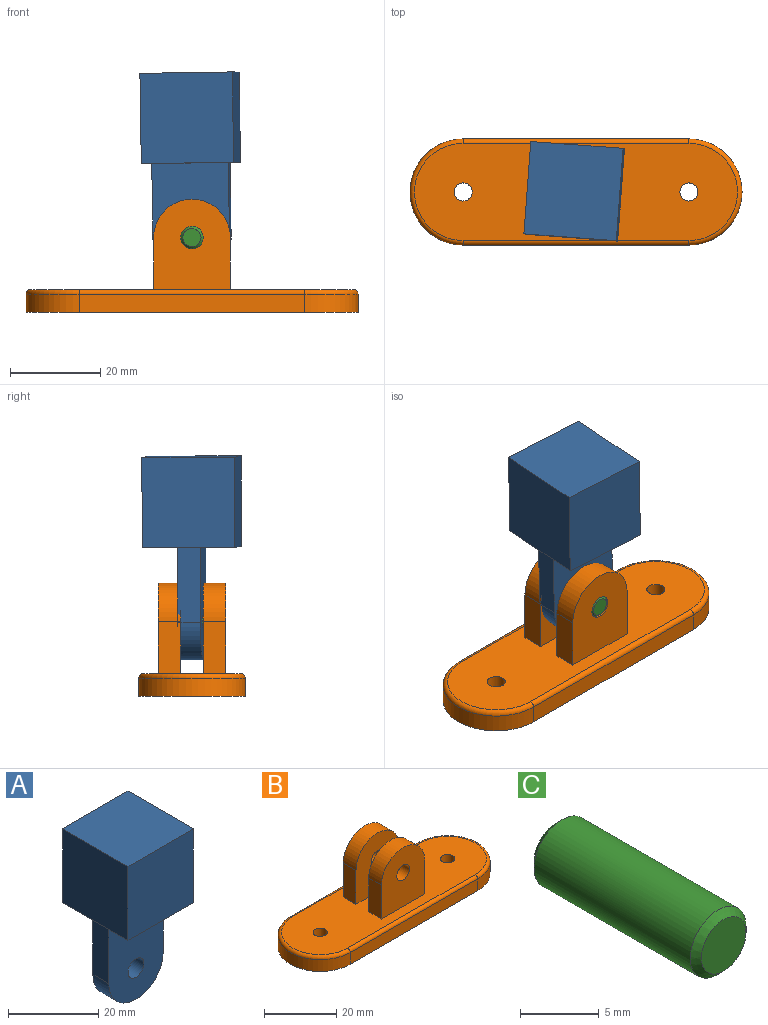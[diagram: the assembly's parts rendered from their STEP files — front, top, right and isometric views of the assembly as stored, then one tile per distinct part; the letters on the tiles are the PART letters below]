
ASSEMBLY  parts=3 mates=2
PART A: 12 faces, bbox 20.5x20.5x45 mm
  f0: plane 25x17mm, normal (0,-1,0), area 374.4mm2, adj f2,f3,f4,f10,f11
  f1: plane 25x17mm, normal (0,1,0), area 374.4mm2, adj f2,f3,f4,f10,f11
  f2: plane 16.5x5mm, normal (-1,0,0), area 82.5mm2, adj f0,f1,f4,f10
  f3: plane 16.5x5mm, normal (1,0,0), area 82.5mm2, adj f0,f1,f4,f10
  f4: plane 20.5x20.5mm, normal (0,0,-1), area 335.3mm2, adj f0,f1,f2,f3,f5,f6,f7,f8
  f5: plane 20.5x20mm, normal (0,-1,0), area 410mm2, adj f4,f6,f8,f9
  f6: plane 20.5x20mm, normal (1,0,0), area 410mm2, adj f4,f5,f7,f9
  f7: plane 20.5x20mm, normal (0,1,0), area 410mm2, adj f4,f6,f8,f9
  f8: plane 20.5x20mm, normal (-1,0,0), area 410mm2, adj f4,f5,f7,f9
  f9: plane 20.5x20.5mm, normal (0,0,1), area 420.3mm2, adj f5,f6,f7,f8
  f10: cylinder r=8.5mm len=17mm, axis (0,1,0), area 133.5mm2, adj f0,f1,f2,f3
  f11: cylinder r=2.5mm len=5mm, axis (0,1,0), area 78.5mm2, adj f0,f1
PART B: 24 faces, bbox 75.4x25.4x25 mm
  f0: plane 20x17mm, normal (0,-1,0), area 289.4mm2, adj f2,f3,f10,f21,f23
  f1: plane 20x17mm, normal (0,1,0), area 289.4mm2, adj f10,f17,f19,f20,f22
  f2: plane 11.5x5mm, normal (-1,0,0), area 57.5mm2, adj f0,f10,f16,f21
  f3: plane 11.5x5mm, normal (1,0,0), area 57.5mm2, adj f0,f10,f16,f21
  f4: plane 50x4mm, normal (0,1,0), area 200mm2, adj f5,f8,f11,f12
  f5: cylinder r=11.75mm len=23.5mm, axis (0,0,-1), area 147.7mm2, adj f4,f6,f11,f14
  f6: plane 50x4mm, normal (0,-1,0), area 200mm2, adj f5,f8,f11,f15
  f7: cylinder r=2mm len=5mm, axis (0,0,-1), area 62.8mm2, adj f10,f11
  f8: cylinder r=11.75mm len=23.5mm, axis (0,0,-1), area 147.7mm2, adj f4,f6,f11,f13
  f9: cylinder r=2mm len=5mm, axis (0,0,-1), area 62.8mm2, adj f10,f11
  f10: plane 71.5x21.5mm, normal (0,0,1), area 1242.9mm2, adj f0,f1,f2,f3,f7,f9,f12,f13
  f11: plane 73.5x23.5mm, normal (0,0,-1), area 1583.6mm2, adj f4,f5,f6,f7,f8,f9
  f12: cylinder r=1mm len=50mm, axis (1,0,0), area 78.5mm2, adj f4,f10,f13,f14
  f13: torus R=10.75mm, axis (0,0,1), area 56.2mm2, adj f8,f10,f12,f15
  f14: torus R=10.75mm, axis (0,0,1), area 56.2mm2, adj f5,f10,f12,f15
  f15: cylinder r=1mm len=50mm, axis (-1,0,0), area 78.5mm2, adj f6,f10,f13,f14
  f16: plane 20x17mm, normal (0,1,0), area 289.4mm2, adj f2,f3,f10,f21,f23
  f17: plane 11.5x5mm, normal (1,0,0), area 57.5mm2, adj f1,f10,f18,f20
  f18: plane 20x17mm, normal (0,-1,0), area 289.4mm2, adj f10,f17,f19,f20,f22
  f19: plane 11.5x5mm, normal (-1,0,0), area 57.5mm2, adj f1,f10,f18,f20
  f20: cylinder r=8.5mm len=17mm, axis (0,-1,0), area 133.5mm2, adj f1,f17,f18,f19
  f21: cylinder r=8.5mm len=17mm, axis (0,-1,0), area 133.5mm2, adj f0,f2,f3,f16
  f22: cylinder r=2.5mm len=5mm, axis (0,-1,0), area 78.5mm2, adj f1,f18
  f23: cylinder r=2.5mm len=5mm, axis (0,-1,0), area 78.5mm2, adj f0,f16
PART C: 5 faces, bbox 5x15x5 mm
  f0: plane 4x4mm, normal (0,1,0), area 12.6mm2, adj f4
  f1: plane 4x4mm, normal (0,-1,0), area 12.6mm2, adj f3
  f2: cylinder r=2.5mm len=14mm, axis (0,-1,0), area 219.9mm2, adj f3,f4
  f3: cone r=2mm half-angle=45deg, axis (0,1,0), area 10mm2, adj f1,f2
  f4: cone r=2.5mm half-angle=45deg, axis (0,-1,0), area 10mm2, adj f0,f2
PLACE A rot(axis=(-0.03,-0.2,-0.98),4.3deg) t=(-7.99,-0.61,38.7)mm
PLACE B t=(-7.74,-0.66,5.71)mm fixed
PLACE C t=(-7.74,-0.66,5.71)mm
MATE fastened B.f20 <-> C.f2  axis (0,-1,0) through (-7.74,-8.16,22.21)mm
MATE ball A.f10 <-> C.f2  axis (0.07,1,0) through (-7.74,-0.66,22.21)mm
